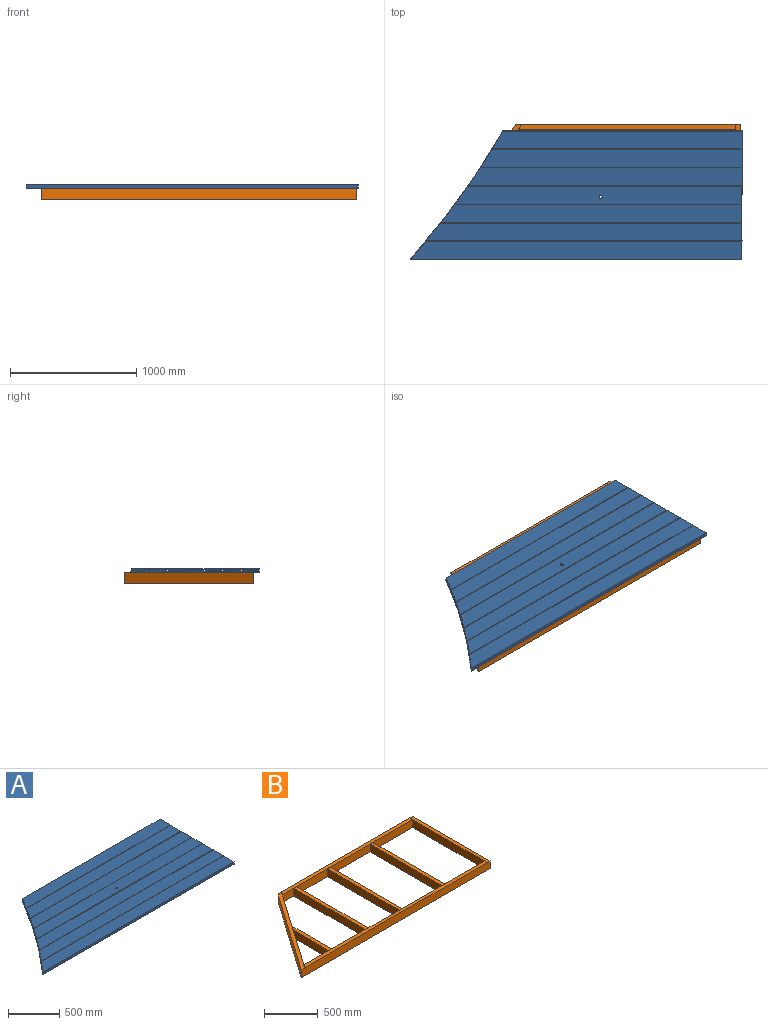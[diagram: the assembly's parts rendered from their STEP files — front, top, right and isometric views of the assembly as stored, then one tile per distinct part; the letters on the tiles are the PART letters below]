
ASSEMBLY  parts=2 mates=1
PART A: 33 faces, bbox 2627.9x1022.4x29.4 mm
  f0: plane 1022.35x29.37mm, normal (1,0,0), area 29037.2mm2, adj f2,f3,f4,f5,f6,f7,f8,f9
  f1: cylinder r=6096mm len=1022.35mm, axis (0,0,-1), area 35886.5mm2, adj f2,f3,f4,f5,f6,f7,f8,f9
  f2: plane 1976.66x139.7mm, normal (0,0,1), area 270282.8mm2, adj f0,f1,f28,f30
  f3: plane 2068.96x139.7mm, normal (0,0,1), area 282796.2mm2, adj f0,f1,f25,f27
  f4: plane 2167.21x139.7mm, normal (0,0,1), area 296120.3mm2, adj f0,f1,f22,f24
  f5: plane 2271.78x139.7mm, normal (0,0,1), area 309795.4mm2, adj f0,f1,f19,f21,f32
  f6: plane 2383.08x139.7mm, normal (0,0,1), area 325395.4mm2, adj f0,f1,f16,f18
  f7: plane 2501.58x139.7mm, normal (0,0,1), area 341462.7mm2, adj f0,f1,f13,f15
  f8: plane 2627.86x139.7mm, normal (0,0,1), area 358577mm2, adj f0,f1,f10,f12
  f9: plane 2627.86x1022.35mm, normal (0,0,-1), area 2281424.8mm2, adj f0,f1,f10,f31,f32
  f10: plane 2627.86x29.37mm, normal (0,-1,0), area 77176.9mm2, adj f0,f1,f8,f9
  f11: plane 2506.91x6.35mm, normal (0,0,1), area 15901.9mm2, adj f0,f1,f12,f13
  f12: plane 2506.91x22.23mm, normal (0,1,0), area 55716mm2, adj f0,f1,f8,f11
  f13: plane 2501.58x22.23mm, normal (0,-1,0), area 55597.6mm2, adj f0,f1,f7,f11
  f14: plane 2388.07x6.35mm, normal (0,0,1), area 15148.4mm2, adj f0,f1,f15,f16
  f15: plane 2388.07x22.23mm, normal (0,1,0), area 53075mm2, adj f0,f1,f7,f14
  f16: plane 2383.08x22.23mm, normal (0,-1,0), area 52963.9mm2, adj f0,f1,f6,f14
  f17: plane 2276.47x6.35mm, normal (0,0,1), area 14440.7mm2, adj f0,f1,f18,f19
  f18: plane 2276.47x22.23mm, normal (0,1,0), area 50594.6mm2, adj f0,f1,f6,f17
  f19: plane 2271.78x22.23mm, normal (0,-1,0), area 50490.3mm2, adj f0,f1,f5,f17
  f20: plane 2171.62x6.35mm, normal (0,0,1), area 13775.8mm2, adj f0,f1,f21,f22
  f21: plane 2171.62x22.23mm, normal (0,1,0), area 48264.3mm2, adj f0,f1,f5,f20
  f22: plane 2167.21x22.23mm, normal (0,-1,0), area 48166.2mm2, adj f0,f1,f4,f20
  f23: plane 2073.1x6.35mm, normal (0,0,1), area 13151mm2, adj f0,f1,f24,f25
  f24: plane 2073.1x22.23mm, normal (0,1,0), area 46074.7mm2, adj f0,f1,f4,f23
  f25: plane 2068.96x22.23mm, normal (0,-1,0), area 45982.5mm2, adj f0,f1,f3,f23
  f26: plane 1980.55x6.35mm, normal (0,0,1), area 12564.1mm2, adj f0,f1,f27,f28
  f27: plane 1980.55x22.23mm, normal (0,1,0), area 44017.7mm2, adj f0,f1,f3,f26
  f28: plane 1976.66x22.23mm, normal (0,-1,0), area 43931.2mm2, adj f0,f1,f2,f26
  f29: plane 1893.66x6.35mm, normal (0,0,1), area 12013.1mm2, adj f0,f1,f30,f31
  f30: plane 1893.66x22.23mm, normal (0,1,0), area 42086.5mm2, adj f0,f1,f2,f29
  f31: plane 1890x7.14mm, normal (0,1,0), area 13501.7mm2, adj f0,f1,f9,f29
  f32: cylinder r=12.7mm len=29.37mm, axis (0,0,1), area 2343.5mm2, adj f5,f9
PART B: 49 faces, bbox 2493.9x1022.4x88.9 mm
  f0: plane 2382.57x88.9mm, normal (0,1,0), area 198648.9mm2, adj f1,f2,f3,f4,f5,f6,f8,f9
  f1: plane 946.15x88.9mm, normal (1,0,0), area 84112.6mm2, adj f0,f7,f10,f24,f43,f44,f45,f46
  f2: plane 946.15x88.9mm, normal (-1,0,0), area 84112.6mm2, adj f0,f7,f10,f24,f43,f44,f45,f46
  f3: plane 946.15x88.9mm, normal (1,0,0), area 84112.6mm2, adj f0,f7,f11,f24,f37,f38,f39,f40
  f4: plane 946.15x88.9mm, normal (-1,0,0), area 84112.6mm2, adj f0,f7,f11,f24,f37,f38,f39,f40
  f5: plane 946.15x88.9mm, normal (1,0,0), area 84112.6mm2, adj f0,f7,f12,f24,f33,f34,f35,f36
  f6: plane 946.15x88.9mm, normal (-1,0,0), area 84112.6mm2, adj f0,f7,f12,f24,f33,f34,f35,f36
  f7: plane 1720.07x88.9mm, normal (0,-1,0), area 143042.8mm2, adj f1,f2,f3,f4,f5,f6,f14,f20
  f8: plane 473.52x88.9mm, normal (-1,0,0), area 42095.3mm2, adj f0,f13,f21,f24,f29,f30,f31,f32
  f9: plane 2409.19x38.1mm, normal (0,0,1), area 91281.9mm2, adj f0,f18,f42,f48
  f10: plane 946.1x38.1mm, normal (0,0,1), area 36046.6mm2, adj f1,f2,f44,f46
  f11: plane 946.1x38.1mm, normal (0,0,1), area 36046.6mm2, adj f3,f4,f38,f40
  f12: plane 946.1x38.1mm, normal (0,0,1), area 36046.6mm2, adj f5,f6,f34,f36
  f13: plane 527.86x38.1mm, normal (0,0,1), area 19074.8mm2, adj f8,f22,f30,f32
  f14: plane 1720.01x38.1mm, normal (0,0,1), area 65024.2mm2, adj f7,f23,f26,f28
  f15: plane 1022.35x762.37mm, normal (0,0,1), area 47551mm2, adj f17,f18,f21,f23
  f16: plane 1022.35x38.1mm, normal (0,0,1), area 38951.5mm2, adj f18,f19,f20,f23
  f17: plane 1022.35x715.86mm, normal (-0.82,0.57,0), area 110952.4mm2, adj f15,f18,f23,f24
  f18: plane 2493.86x88.9mm, normal (0,-1,0), area 221703.8mm2, adj f9,f15,f16,f17,f19,f20,f21,f24
  f19: plane 1022.35x88.9mm, normal (1,0,0), area 90886.9mm2, adj f16,f18,f23,f24
  f20: plane 1022.35x88.9mm, normal (-1,0,0), area 84306.3mm2, adj f0,f7,f16,f18,f23,f24,f27,f47
  f21: plane 1022.35x715.86mm, normal (0.82,-0.57,0), area 97182.5mm2, adj f0,f7,f8,f15,f18,f22,f23,f24
  f22: plane 527.93x88.9mm, normal (1,0,0), area 46932.6mm2, adj f0,f13,f21,f24,f29,f30,f31,f32
  f23: plane 1778x88.9mm, normal (0,1,0), area 158064.1mm2, adj f14,f15,f16,f17,f19,f20,f21,f24
  f24: plane 2493.86x1022.35mm, normal (0,0,-1), area 370035.4mm2, adj f0,f1,f2,f3,f4,f5,f6,f7
  f25: plane 38.1x26.71mm, normal (0,0,1), area 1.2mm2, adj f7,f21,f23,f26
  f26: plane 38.1x26.68mm, normal (-0.82,0.57,0), area 118.1mm2, adj f7,f14,f23,f25
  f27: plane 38.1x0.03mm, normal (0,0,1), area 1mm2, adj f7,f20,f23,f28
  f28: plane 38.1x2.54mm, normal (1,0,0), area 96.8mm2, adj f7,f14,f23,f27
  f29: plane 54.46x38.1mm, normal (0,0,1), area 1.7mm2, adj f8,f21,f22,f30
  f30: plane 54.41x38.1mm, normal (-0.82,0.57,0), area 168.7mm2, adj f8,f13,f22,f29
  f31: plane 38.1x0.03mm, normal (0,0,1), area 1mm2, adj f0,f8,f22,f32
  f32: plane 38.1x2.54mm, normal (0,-1,0), area 96.8mm2, adj f8,f13,f22,f31
  f33: plane 38.1x0.02mm, normal (0,0,1), area 0.8mm2, adj f5,f6,f7,f34
  f34: plane 38.1x2.54mm, normal (0,1,0), area 96.8mm2, adj f5,f6,f12,f33
  f35: plane 38.1x0.03mm, normal (0,0,1), area 1mm2, adj f0,f5,f6,f36
  f36: plane 38.1x2.54mm, normal (0,-1,0), area 96.8mm2, adj f5,f6,f12,f35
  f37: plane 38.1x0.02mm, normal (0,0,1), area 0.8mm2, adj f3,f4,f7,f38
  f38: plane 38.1x2.54mm, normal (0,1,0), area 96.8mm2, adj f3,f4,f11,f37
  f39: plane 38.1x0.03mm, normal (0,0,1), area 1mm2, adj f0,f3,f4,f40
  f40: plane 38.1x2.54mm, normal (0,-1,0), area 96.8mm2, adj f3,f4,f11,f39
  f41: plane 38.1x26.71mm, normal (0,0,1), area 1.2mm2, adj f0,f18,f21,f42
  f42: plane 38.1x26.68mm, normal (-0.82,0.57,0), area 118.1mm2, adj f0,f9,f18,f41
  f43: plane 38.1x0.02mm, normal (0,0,1), area 0.8mm2, adj f1,f2,f7,f44
  f44: plane 38.1x2.54mm, normal (0,1,0), area 96.8mm2, adj f1,f2,f10,f43
  f45: plane 38.1x0.03mm, normal (0,0,1), area 1mm2, adj f0,f1,f2,f46
  f46: plane 38.1x2.54mm, normal (0,-1,0), area 96.8mm2, adj f1,f2,f10,f45
  f47: plane 38.1x0.03mm, normal (0,0,1), area 1mm2, adj f0,f18,f20,f48
  f48: plane 38.1x2.54mm, normal (1,0,0), area 96.8mm2, adj f0,f9,f18,f47
PLACE A t=(1237.05,1336.65,88.9)mm
PLACE B t=(1496.11,1912.37,0)mm
MATE fastened B.f16 <-> A.f9  axis (0,0,1) through (1164.68,557.58,88.9)mm
